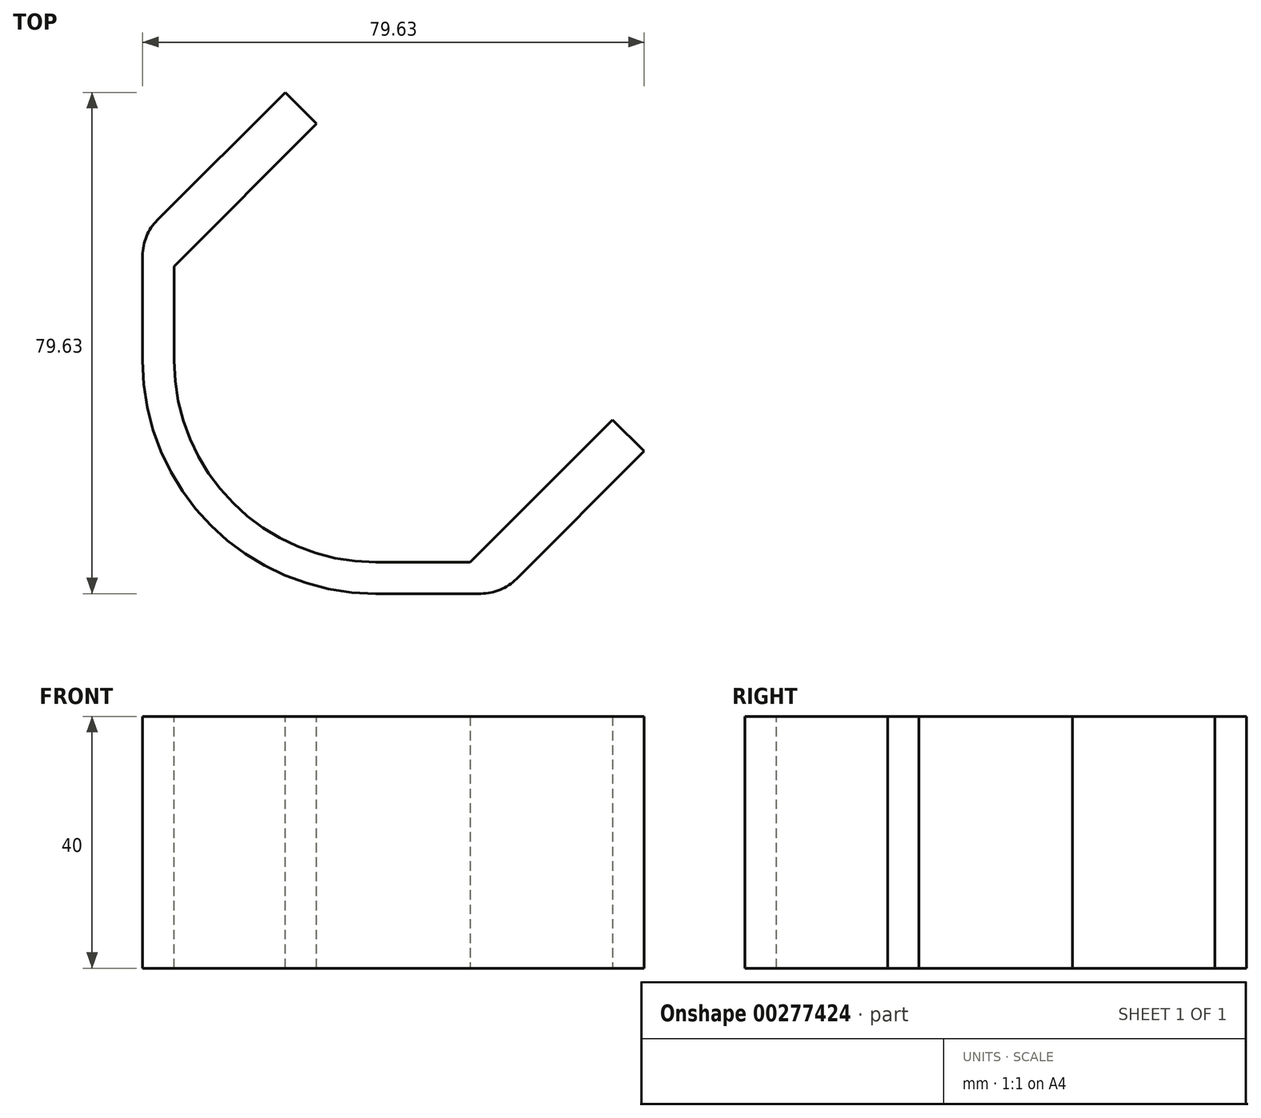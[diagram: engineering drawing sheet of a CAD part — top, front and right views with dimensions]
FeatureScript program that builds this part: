
annotation { "Feature Type Name" : "Feature", "Feature Type Description" : "" }
export const myFeature = defineFeature(function(context is Context, id is Id, definition is map)
    precondition{}
    {
        {
            var Q0;
            Q0=qCreatedBy(makeId("Front.planeOp"),FACE);
            var sketch = newSketch(context, id + "F0", { "sketchPlane" : qUnion([Q0])});
            skLineSegment(sketch, "E0", {"start": v(0, 0) * mm, "end": v(0, 44.79) * mm});
            skLineSegment(sketch, "E1.bottom", {"start": v(-32, 0) * mm, "end": v(-37, 0) * mm});
            skLineSegment(sketch, "E1.top", {"start": v(-32, 40) * mm, "end": v(-37, 40) * mm});
            skLineSegment(sketch, "E1.left", {"start": v(-32, 0) * mm, "end": v(-32, 40) * mm});
            skLineSegment(sketch, "E1.right", {"start": v(-37, 0) * mm, "end": v(-37, 40) * mm});
            skSolve(sketch);
        }
        {
            var Q0;
            Q0=makeQuery(id+"F0.imprint","IMPRINT",FACE,{"disambiguationData":[TD([[makeQuery(id+"F0.imprint","IMPRINT",EDGE,{"derivedFrom":sQuery(id+"F0.wireOp",EDGE,"E1.bottom")}),-1.0]])]});
            var Q1;
            Q1=sQuery(id+"F0.wireOp",EDGE,"E0");
            revolve(context, id + "F1", {"entities" : qUnion([Q0]), "axis" : qUnion([Q1]), "revolveType" : RevolveType.ONE_DIRECTION, "angle" : 90 * degree});
        }
        {
            var Q0;
            Q0=makeQuery(id+"F1.opRevolve","CAP_FACE",FACE,{"disambiguationData":[OSD([sQuery(id+"F0.wireOp",EDGE,"E1.bottom"),sQuery(id+"F0.wireOp",EDGE,"E1.top"),sQuery(id+"F0.wireOp",EDGE,"E1.left"),sQuery(id+"F0.wireOp",EDGE,"E1.right")])],"isStart":false});
            extrude(context, id + "F2", {"entities" : qUnion([Q0]), "operationType" : NewBodyOperationType.ADD, "depth" : 20 * mm});
        }
        {
            var Q0;
            Q0=makeQuery(id+"F1.opRevolve","CAP_FACE",FACE,{"disambiguationData":[OSD([sQuery(id+"F0.wireOp",EDGE,"E1.bottom"),sQuery(id+"F0.wireOp",EDGE,"E1.top"),sQuery(id+"F0.wireOp",EDGE,"E1.left"),sQuery(id+"F0.wireOp",EDGE,"E1.right")])],"isStart":true});
            extrude(context, id + "F3", {"entities" : qUnion([Q0]), "operationType" : NewBodyOperationType.ADD, "depth" : 20 * mm});
        }
        {
            var Q0;
            Q0=makeQuery(id+"F2.opExtrude","CAP_EDGE",EDGE,{"disambiguationData":[OSD([sQuery(id+"F0.wireOp",EDGE,"E1.left")])],"isStart":false});
            var Q1;
            Q1=makeQuery(id+"F3.opExtrude","CAP_EDGE",EDGE,{"disambiguationData":[OSD([sQuery(id+"F0.wireOp",EDGE,"E1.left")])],"isStart":false});
            chamfer(context, id + "F4", {"entities" : qUnion([Q0, Q1]), "width" : 5 * mm, "tangentPropagation" : true});
        }
        {
            var Q0;
            {var subQ0=sQuery(id+"F0.wireOp",EDGE,"E1.left");Q0=makeQuery(id+"F4.opChamfer","BLEND_FACE",FACE,{"disambiguationData":[OSD([subQ0]),TDD([makeQuery(id+"F2.opExtrude","CAP_EDGE",EDGE,{"disambiguationData":[OSD([subQ0])],"isStart":false})])]});}
            var Q1;
            {var subQ0=sQuery(id+"F0.wireOp",EDGE,"E1.left");Q1=makeQuery(id+"F4.opChamfer","BLEND_FACE",FACE,{"disambiguationData":[OSD([subQ0]),TDD([makeQuery(id+"F3.opExtrude","CAP_EDGE",EDGE,{"disambiguationData":[OSD([subQ0])],"isStart":false})])]});}
            extrude(context, id + "F5", {"entities" : qUnion([Q0, Q1]), "operationType" : NewBodyOperationType.ADD, "depth" : 32 * mm});
        }
        {
            var Q0;
            {var subQ0=sQuery(id+"F0.wireOp",EDGE,"E1.right");var subQ1=sQuery(id+"F0.wireOp",EDGE,"E1.left");var subQ2=makeQuery(id+"F4.opChamfer","BLEND_EDGE",EDGE,{"blendedFrom":[makeQuery(id+"F3.opExtrude","CAP_EDGE",EDGE,{"disambiguationData":[OSD([subQ1])],"isStart":false}),makeQuery(id+"F3.opExtrude","SWEPT_FACE",FACE,{"disambiguationData":[OSD([subQ0])]})],"blendedInto":[makeQuery(id+"F3.opExtrude","SWEPT_FACE",FACE,{"disambiguationData":[OSD([subQ0])]})]});Q0=makeQuery(id+"F5.boolean.opBoolean","MERGE",EDGE,{"derivedFrom":[subQ2,makeQuery(id+"F5.opExtrude","CAP_EDGE",EDGE,{"disambiguationData":[OSD([subQ1,subQ0]),TDD([subQ2])],"isStart":true})]});}
            var Q1;
            {var subQ0=sQuery(id+"F0.wireOp",EDGE,"E1.right");Q1=makeQuery(id+"F3.boolean.opBoolean","MERGE",EDGE,{"derivedFrom":[makeQuery(id+"F1.opRevolve","CAP_EDGE",EDGE,{"disambiguationData":[OSD([subQ0])],"isStart":true}),makeQuery(id+"F3.opExtrude","CAP_EDGE",EDGE,{"disambiguationData":[OSD([subQ0])],"isStart":true})]});}
            var Q2;
            {var subQ0=sQuery(id+"F0.wireOp",EDGE,"E1.right");Q2=makeQuery(id+"F2.boolean.opBoolean","MERGE",EDGE,{"derivedFrom":[makeQuery(id+"F1.opRevolve","CAP_EDGE",EDGE,{"disambiguationData":[OSD([subQ0])],"isStart":false}),makeQuery(id+"F2.opExtrude","CAP_EDGE",EDGE,{"disambiguationData":[OSD([subQ0])],"isStart":true})]});}
            var Q3;
            {var subQ0=sQuery(id+"F0.wireOp",EDGE,"E1.right");var subQ1=sQuery(id+"F0.wireOp",EDGE,"E1.left");var subQ2=makeQuery(id+"F4.opChamfer","BLEND_EDGE",EDGE,{"blendedFrom":[makeQuery(id+"F2.opExtrude","CAP_EDGE",EDGE,{"disambiguationData":[OSD([subQ1])],"isStart":false}),makeQuery(id+"F2.opExtrude","SWEPT_FACE",FACE,{"disambiguationData":[OSD([subQ0])]})],"blendedInto":[makeQuery(id+"F2.opExtrude","SWEPT_FACE",FACE,{"disambiguationData":[OSD([subQ0])]})]});Q3=makeQuery(id+"F5.boolean.opBoolean","MERGE",EDGE,{"derivedFrom":[subQ2,makeQuery(id+"F5.opExtrude","CAP_EDGE",EDGE,{"disambiguationData":[OSD([subQ1,subQ0]),TDD([subQ2])],"isStart":true})]});}
            fillet(context, id + "F6", {"entities" : qUnion([Q0, Q1, Q2, Q3]), "radius" : 8 * mm, "tangentPropagation" : true, "allowEdgeOverflow" : false});
        }
    });
